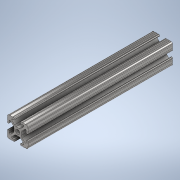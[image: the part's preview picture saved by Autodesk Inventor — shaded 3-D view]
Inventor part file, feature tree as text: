
AUTODESK INVENTOR PART (.ipt)
format: ipt  version: 2020 (Build 240168000, 168)  size: 238,592 bytes
history: native  units: in
note: dims shown in document units (in); Inventor stores cm internally (conversion verified against a paired STEP export)
features: extrude x1, sketch x1
ambient origin geometry x8: Origin, YZ Plane, XZ Plane, XY Plane, X Axis, Y Axis, Z Axis, Center Point
bodies: Solid1 (feature_tree)
feature tree (2):
  extrude  "Extrusion1"  [1 undecoded]
  sketch  "Sketch1"  dims[d0=7.0in d1=0.0in]
note: 1 required parameter value undecoded (feature->parameter linkage not recoverable at this tier; creation-order binding heuristic only, values carry confidence <= 0.55)
